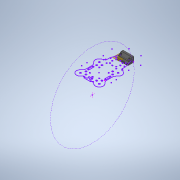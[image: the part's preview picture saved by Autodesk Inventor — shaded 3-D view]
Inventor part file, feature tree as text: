
AUTODESK INVENTOR PART (.ipt)
format: ipt  version: 2020 (Build 240168000, 168)  size: 543,744 bytes
history: native  units: in
note: dims shown in document units (in); Inventor stores cm internally (conversion verified against a paired STEP export)
features: sketch x10, extrude x9, plane x6, fillet x5, projected_geometry x5
ambient origin geometry x8: Origin, YZ Plane, XZ Plane, XY Plane, X Axis, Y Axis, Z Axis, Center Point
bodies: Solid2 (feature_tree)
feature tree (35):
  plane  "Work Plane1"
  plane  "Work Plane7"
  plane  "Work Plane4"
  plane  "Work Plane9"
  sketch  "Sketch13"  dims[d22=0.1181in d23=0.0in d24=0.2008in]
  plane  "Work Plane11"
  extrude  "Extrusion10"  Depth=0.2008in
  plane  "Work Plane8"
  sketch  "Sketch15"  dims[d35=0.0001in d36=1.378in d37=0.0in]
  extrude  "Extrusion12"  Depth=1.378in TaperAngle=0.0deg
  extrude  "Extrusion13"  Depth=1.378in TaperAngle=0.0deg
  extrude  "Extrusion14"  Depth=0.2165in
  extrude  "Extrusion15"  Depth=1.378in TaperAngle=0.0deg
  extrude  "Extrusion16"  Depth=0.1181in
  extrude  "Extrusion17"  Depth=0.1181in TaperAngle=0.0deg
  extrude  "Extrusion18"  Depth=0.0394in TaperAngle=0.0deg
  extrude  "Extrusion19"  Depth=0.0295in
  fillet  "Fillet1"  Radius=0.1181in
  fillet  "Fillet2"  Radius=0.0394in
  fillet  "Fillet3"  Radius=0.0394in
  fillet  "Fillet4"  Radius=0.0197in
  fillet  "Fillet5"  Radius=1.9685in
  sketch  "Sketch14"  dims[d25=0.2008in d32=1.378in d33=0.0in]
  sketch  "Sketch17"  dims[d38=0.0in d39=0.0in d40=0.2165in]
  sketch  "Sketch18"  dims[d41=0.2165in d42=1.378in d43=0.0in]
  projected_geometry  "Projected Loop7"
  projected_geometry  "Projected Loop8"
  sketch  "Sketch19"  dims[d44=0.1181in d45=0.0in d46=0.1181in]
  sketch  "Sketch20"  dims[d47=0.1181in d48=0.1181in d49=0.0in]
  sketch  "Sketch21"  dims[d50=0.0394in d51=0.0in d52=0.0394in d53=0.0in]
  sketch  "Sketch22"  dims[d54=0.1969in d55=0.0295in d56=0.1181in d57=0.0394in d58=0.0394in d2=0.0197in d3=1.9685in]
  projected_geometry  "Projected Loop9"
  sketch  "Sketch23"  dims[d4=0.0197in d5=1.9685in d11=0.0197in d12=1.9685in d13=0.0197in d14=1.9685in d34=0.0197in]
  projected_geometry  "Projected Loop10"
  projected_geometry  "Projected Loop11"
